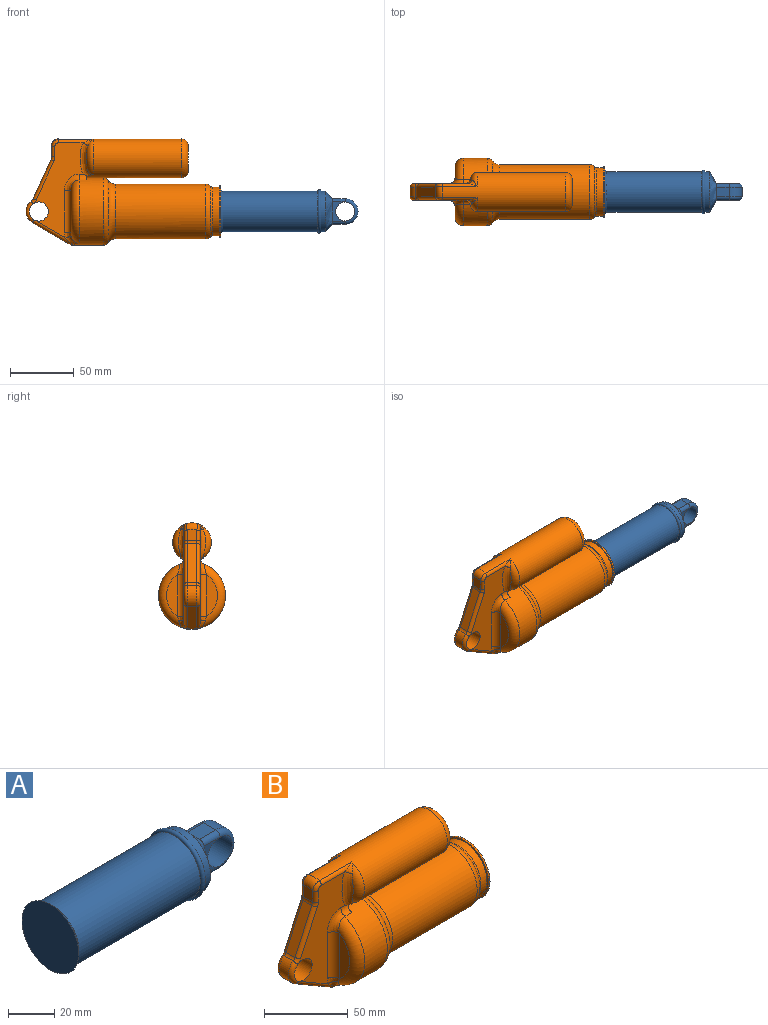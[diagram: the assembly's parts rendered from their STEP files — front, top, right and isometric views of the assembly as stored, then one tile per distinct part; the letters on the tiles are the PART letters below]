
ASSEMBLY  parts=2 mates=1
PART A: 18 faces, bbox 109.6x37.9x37.9 mm
  f0: cylinder r=15.88mm len=31.75mm, axis (-1,0,0), area 380mm2, adj f1,f17
  f1: torus R=15.88mm, axis (-1,0,0), area 418.2mm2, adj f0,f2
  f2: cylinder r=15.88mm len=74.61mm, axis (-1,0,0), area 7442.3mm2, adj f1,f3
  f3: cone r=17.46mm half-angle=45deg, axis (-1,0,0), area 235.1mm2, adj f2,f4
  f4: plane 34.93x34.93mm, normal (-1,0,0), area 958mm2, adj f3
  f5: plane 10.32x7.87mm, normal (0,0,-1), area 76.7mm2, adj f6,f13,f16,f17
  f6: cylinder r=10.07mm len=20.14mm, axis (0,1,0), area 241.1mm2, adj f5,f8,f12,f15
  f7: cylinder r=7.53mm len=15.06mm, axis (0,1,0), area 601mm2, adj f9,f10,f12,f15
  f8: plane 10.32x7.87mm, normal (0,0,1), area 76.7mm2, adj f6,f11,f14,f17
  f9: plane 15.87x10.88mm, normal (0,-1,0), area 62.6mm2, adj f7,f14,f16,f17
  f10: plane 15.87x10.88mm, normal (0,1,0), area 62.6mm2, adj f7,f11,f13,f17
  f11: cylinder r=2.54mm len=10.07mm, axis (-1,0,0), area 40.2mm2, adj f8,f10,f12,f17
  f12: torus R=7.53mm, axis (0,-1,0), area 114.7mm2, adj f6,f7,f11,f13
  f13: cylinder r=2.54mm len=10.07mm, axis (1,0,0), area 40.2mm2, adj f5,f10,f12,f17
  f14: cylinder r=2.54mm len=10.07mm, axis (1,0,0), area 40.2mm2, adj f8,f9,f15,f17
  f15: torus R=7.53mm, axis (0,-1,0), area 114.7mm2, adj f6,f7,f14,f16
  f16: cylinder r=2.54mm len=10.07mm, axis (-1,0,0), area 40.2mm2, adj f5,f9,f15,f17
  f17: bspline ~31.73x31.72mm, area 687.9mm2, adj f0,f5,f8,f9,f10,f11,f13,f14
PART B: 64 faces, bbox 154.5x60.6x88.8 mm
  f0: plane 19.17x3.51mm, normal (1,0,0), area 17mm2, adj f2,f27,f54,f59
  f1: plane 32.99x8.64mm, normal (-1,0,0), area 199.9mm2, adj f25,f52
  f2: cylinder r=26.42mm len=52.83mm, axis (-1,0,0), area 3136.9mm2, adj f0,f11,f15,f16,f24,f25,f34,f42
  f3: plane 32.99x8.64mm, normal (-1,0,0), area 199.9mm2, adj f24,f57
  f4: plane 40.64x40.64mm, normal (1,0,0), area 337.8mm2, adj f5,f13
  f5: cylinder r=20.32mm len=40.64mm, axis (-1,0,0), area 162.1mm2, adj f4,f6
  f6: plane 40.64x40.64mm, normal (-1,0,0), area 157.1mm2, adj f5,f7
  f7: cylinder r=19.05mm len=38.1mm, axis (-1,0,0), area 615.4mm2, adj f6,f9
  f8: cylinder r=21.59mm len=71.22mm, axis (-1,0,0), area 9660.9mm2, adj f10,f12
  f9: torus R=21.59mm, axis (-1,0,0), area 259.6mm2, adj f7,f12
  f10: torus R=27.94mm, axis (-1,0,0), area 857.6mm2, adj f8,f11
  f11: torus R=21.34mm, axis (1,0,0), area 782.6mm2, adj f2,f10
  f12: torus R=16.51mm, axis (1,0,0), area 564.1mm2, adj f8,f9
  f13: cylinder r=17.48mm len=76.2mm, axis (1,0,0), area 8366.8mm2, adj f4,f14
  f14: cone r=0mm half-angle=59deg, axis (1,0,0), area 1119.3mm2, adj f13
  f15: plane 5.4x0.66mm, normal (1,0,0), area 0.7mm2, adj f2,f22,f34
  f16: plane 5.4x0.66mm, normal (1,0,0), area 0.7mm2, adj f2,f22,f42
  f17: plane 74.92x39.71mm, normal (0,-1,0), area 1328.9mm2, adj f23,f42,f44,f45,f46,f47,f48,f49
  f18: plane 74.92x39.71mm, normal (0,1,0), area 1328.9mm2, adj f23,f34,f36,f37,f38,f39,f40,f41
  f19: plane 9.05x7.62mm, normal (-1,0,0), area 67.1mm2, adj f30,f32,f39,f47
  f20: plane 30.89x14.17mm, normal (-0.91,0,0.42), area 259mm2, adj f32,f33,f37,f45
  f21: cylinder r=10.07mm len=16.77mm, axis (0,1,0), area 151.4mm2, adj f22,f33,f35,f43
  f22: plane 30.46x17.71mm, normal (-0.5,0,-0.86), area 268.5mm2, adj f15,f16,f21,f34,f42
  f23: cylinder r=7.53mm len=15.06mm, axis (0,1,0), area 601mm2, adj f17,f18,f35,f43
  f24: torus R=20.07mm, axis (1,0,0), area 549.9mm2, adj f2,f3,f55,f56,f58
  f25: torus R=20.07mm, axis (1,0,0), area 549.9mm2, adj f1,f2,f50,f51,f53
  f26: plane 20.32x20.32mm, normal (1,0,0), area 324.3mm2, adj f31
  f27: cylinder r=15.24mm len=97.32mm, axis (-1,0,0), area 7020.9mm2, adj f0,f28,f29,f30,f31,f41,f49,f54
  f28: torus R=10.16mm, axis (-1,0,0), area 163.2mm2, adj f27,f62,f63
  f29: torus R=10.16mm, axis (-1,0,0), area 163.2mm2, adj f27,f60,f61
  f30: torus R=10.16mm, axis (-1,0,0), area 73.1mm2, adj f19,f27,f40,f48
  f31: torus R=10.16mm, axis (1,0,0), area 671.5mm2, adj f26,f27
  f32: cylinder r=5.08mm len=7.62mm, axis (0,-1,0), area 16.6mm2, adj f19,f20,f38,f46
  f33: cylinder r=5.08mm len=7.62mm, axis (0,1,0), area 19.3mm2, adj f20,f21,f36,f44
  f34: cylinder r=2.54mm len=32.52mm, axis (0.86,0,-0.5), area 137.2mm2, adj f2,f15,f18,f22,f35,f50
  f35: torus R=7.53mm, axis (0,-1,0), area 72mm2, adj f21,f23,f34,f36
  f36: torus R=7.62mm, axis (0,-1,0), area 11.9mm2, adj f18,f33,f35,f37
  f37: cylinder r=2.54mm len=31.95mm, axis (-0.42,0,-0.91), area 135.6mm2, adj f18,f20,f36,f38
  f38: torus R=7.62mm, axis (0,-1,0), area 10.3mm2, adj f18,f32,f37,f39
  f39: cylinder r=2.54mm len=8.31mm, axis (0,0,-1), area 33.2mm2, adj f18,f19,f38,f40
  f40: bspline ~6.22x5.44mm, area 22.4mm2, adj f18,f30,f39,f41
  f41: cylinder r=2.54mm len=27.47mm, axis (-1,0,0), area 75.8mm2, adj f18,f27,f40,f61
  f42: cylinder r=2.54mm len=32.52mm, axis (-0.86,0,0.5), area 137.2mm2, adj f2,f16,f17,f22,f43,f55
  f43: torus R=7.53mm, axis (0,-1,0), area 72mm2, adj f21,f23,f42,f44
  f44: torus R=7.62mm, axis (0,-1,0), area 11.9mm2, adj f17,f33,f43,f45
  f45: cylinder r=2.54mm len=31.95mm, axis (0.42,0,0.91), area 135.6mm2, adj f17,f20,f44,f46
  f46: torus R=7.62mm, axis (0,-1,0), area 10.3mm2, adj f17,f32,f45,f47
  f47: cylinder r=2.54mm len=8.31mm, axis (0,0,1), area 33.2mm2, adj f17,f19,f46,f48
  f48: bspline ~6.22x5.44mm, area 22.4mm2, adj f17,f30,f47,f49
  f49: cylinder r=2.54mm len=27.47mm, axis (-1,0,0), area 75.8mm2, adj f17,f27,f48,f63
  f50: bspline ~12.78x10mm, area 40.6mm2, adj f2,f25,f34,f51
  f51: bspline ~8.1x5.97mm, area 26.7mm2, adj f18,f25,f50,f52
  f52: cylinder r=5.08mm len=32.99mm, axis (0,0,1), area 263.2mm2, adj f1,f18,f51,f53
  f53: bspline ~17.38x12.64mm, area 98.6mm2, adj f18,f25,f52,f54
  f54: cylinder r=5.08mm len=6.16mm, axis (-1,0,0), area 34.6mm2, adj f0,f2,f18,f27,f53,f60
  f55: bspline ~12.78x10mm, area 40.6mm2, adj f2,f24,f42,f56
  f56: bspline ~8.1x5.97mm, area 26.7mm2, adj f17,f24,f55,f57
  f57: cylinder r=5.08mm len=32.99mm, axis (0,0,-1), area 263.2mm2, adj f3,f17,f56,f58
  f58: bspline ~17.38x12.64mm, area 98.6mm2, adj f17,f24,f57,f59
  f59: cylinder r=5.08mm len=6.16mm, axis (-1,0,0), area 34.6mm2, adj f0,f2,f17,f27,f58,f62
  f60: bspline ~29.34x10.67mm, area 166.5mm2, adj f18,f27,f29,f54,f61
  f61: bspline ~8.72x5.83mm, area 13.3mm2, adj f29,f41,f60
  f62: bspline ~30.12x11.76mm, area 166.5mm2, adj f17,f27,f28,f59,f63
  f63: bspline ~8.72x5.83mm, area 13.3mm2, adj f28,f49,f62
PLACE A t=(107.56,-0.27,16.29)mm
PLACE B t=(0.54,-0.27,-0.86)mm fixed
MATE slider A.f0 <-> B.f2  axis (-1,0,0) through (143.96,-0.27,-0.86)mm
